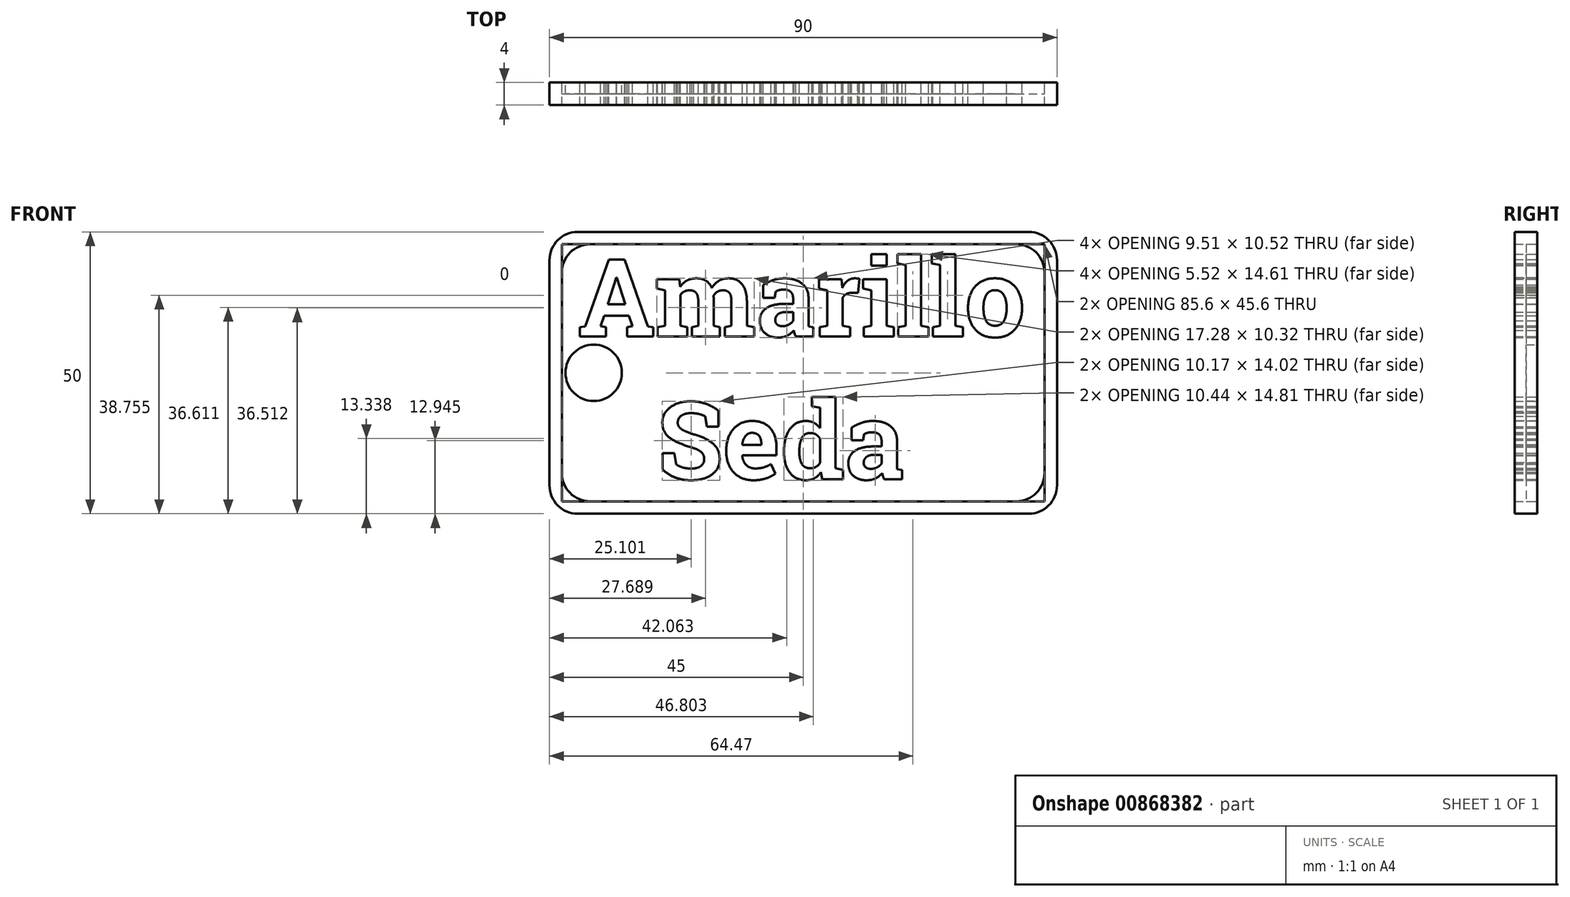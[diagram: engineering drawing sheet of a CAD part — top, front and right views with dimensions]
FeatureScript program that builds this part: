
annotation { "Feature Type Name" : "Feature", "Feature Type Description" : "" }
export const myFeature = defineFeature(function(context is Context, id is Id, definition is map)
    precondition{}
    {
        {
            var Q0;
            Q0=qCreatedBy(makeId("Front.planeOp"),FACE);
            var sketch = newSketch(context, id + "F0", { "sketchPlane" : qUnion([Q0])});
            skLineSegment(sketch, "E0.bottom", {"start": v(-45, 25) * mm, "end": v(45, 25) * mm});
            skLineSegment(sketch, "E0.top", {"start": v(-45, -25) * mm, "end": v(45, -25) * mm});
            skLineSegment(sketch, "E0.left", {"start": v(-45, 25) * mm, "end": v(-45, -25) * mm});
            skLineSegment(sketch, "E0.right", {"start": v(45, 25) * mm, "end": v(45, -25) * mm});
            skLineSegment(sketch, "E1.0", {"start": v(-42.8, 22.8) * mm, "end": v(42.8, 22.8) * mm});
            skLineSegment(sketch, "E1.1", {"start": v(-42.8, 22.8) * mm, "end": v(-42.8, -22.8) * mm});
            skLineSegment(sketch, "E1.2", {"start": v(-42.8, -22.8) * mm, "end": v(42.8, -22.8) * mm});
            skLineSegment(sketch, "E1.3", {"start": v(42.8, 22.8) * mm, "end": v(42.8, -22.8) * mm});
            skText(sketch, "E2", { "text": "Amarillo\n   Seda", "fontName": "RobotoSlab-Bold.ttf"});
            skCircle(sketch, "E3", {"center": v(-37.16, 0) * mm, "radius": 5 * mm});
            const initialGuessF0  = {"E2": [-0.04, 0.00645, 1, 0, 0.01381]};
            skSetInitialGuess(sketch, initialGuessF0);
            skSolve(sketch);
        }
        {
            var Q0;
            Q0=makeQuery(id+"F0.imprint","IMPRINT",FACE,{"disambiguationData":[TD([[makeQuery(id+"F0.imprint","IMPRINT",EDGE,{"derivedFrom":sQuery(id+"F0.wireOp",EDGE,"E2.sketch_text.stroke-16")}),1.0]])]});
            var Q1;
            Q1=makeQuery(id+"F0.imprint","IMPRINT",FACE,{"disambiguationData":[TD([[makeQuery(id+"F0.imprint","IMPRINT",EDGE,{"derivedFrom":sQuery(id+"F0.wireOp",EDGE,"E2.sketch_text.stroke-90")}),1.0]])]});
            var Q2;
            Q2=makeQuery(id+"F0.imprint","IMPRINT",FACE,{"disambiguationData":[TD([[makeQuery(id+"F0.imprint","IMPRINT",EDGE,{"derivedFrom":sQuery(id+"F0.wireOp",EDGE,"E2.sketch_text.stroke-161")}),1.0]])]});
            var Q3;
            Q3=makeQuery(id+"F0.imprint","IMPRINT",FACE,{"disambiguationData":[TD([[makeQuery(id+"F0.imprint","IMPRINT",EDGE,{"derivedFrom":sQuery(id+"F0.wireOp",EDGE,"E2.sketch_text.stroke-281")}),1.0]])]});
            var Q4;
            Q4=makeQuery(id+"F0.imprint","IMPRINT",FACE,{"disambiguationData":[TD([[makeQuery(id+"F0.imprint","IMPRINT",EDGE,{"derivedFrom":sQuery(id+"F0.wireOp",EDGE,"E2.sketch_text.stroke-244")}),1.0]])]});
            var Q5;
            Q5=makeQuery(id+"F0.imprint","IMPRINT",FACE,{"disambiguationData":[TD([[makeQuery(id+"F0.imprint","IMPRINT",EDGE,{"derivedFrom":sQuery(id+"F0.wireOp",EDGE,"E2.sketch_text.stroke-218")}),1.0]])]});
            var Q6;
            Q6=makeQuery(id+"F0.imprint","IMPRINT",FACE,{"disambiguationData":[TD([[makeQuery(id+"F0.imprint","IMPRINT",EDGE,{"derivedFrom":sQuery(id+"F0.wireOp",EDGE,"E1.0")}),-1.0]])]});
            extrude(context, id + "F1", {"entities" : qUnion([Q0, Q1, Q2, Q3, Q4, Q5, Q6]), "depth" : 2 * mm, "offsetDistance" : 25 * mm});
        }
        {
            var Q0;
            Q0=makeQuery(id+"F0.imprint","IMPRINT",FACE,{"disambiguationData":[TD([[makeQuery(id+"F0.imprint","IMPRINT",EDGE,{"derivedFrom":sQuery(id+"F0.wireOp",EDGE,"E2.sketch_text.stroke-0")}),-1.0]])]});
            var Q1;
            Q1=makeQuery(id+"F0.imprint","IMPRINT",FACE,{"disambiguationData":[TD([[makeQuery(id+"F0.imprint","IMPRINT",EDGE,{"derivedFrom":sQuery(id+"F0.wireOp",EDGE,"E2.sketch_text.stroke-20")}),-1.0]])]});
            var Q2;
            Q2=makeQuery(id+"F0.imprint","IMPRINT",FACE,{"disambiguationData":[TD([[makeQuery(id+"F0.imprint","IMPRINT",EDGE,{"derivedFrom":sQuery(id+"F0.wireOp",EDGE,"E2.sketch_text.stroke-63")}),-1.0]])]});
            var Q3;
            Q3=makeQuery(id+"F0.imprint","IMPRINT",FACE,{"disambiguationData":[TD([[makeQuery(id+"F0.imprint","IMPRINT",EDGE,{"derivedFrom":sQuery(id+"F0.wireOp",EDGE,"E2.sketch_text.stroke-98")}),-1.0]])]});
            var Q4;
            Q4=makeQuery(id+"F0.imprint","IMPRINT",FACE,{"disambiguationData":[TD([[makeQuery(id+"F0.imprint","IMPRINT",EDGE,{"derivedFrom":sQuery(id+"F0.wireOp",EDGE,"E2.sketch_text.stroke-117")}),-1.0]])]});
            var Q5;
            Q5=makeQuery(id+"F0.imprint","IMPRINT",FACE,{"disambiguationData":[TD([[makeQuery(id+"F0.imprint","IMPRINT",EDGE,{"derivedFrom":sQuery(id+"F0.wireOp",EDGE,"E2.sketch_text.stroke-127")}),-1.0]])]});
            var Q6;
            Q6=makeQuery(id+"F0.imprint","IMPRINT",FACE,{"disambiguationData":[TD([[makeQuery(id+"F0.imprint","IMPRINT",EDGE,{"derivedFrom":sQuery(id+"F0.wireOp",EDGE,"E2.sketch_text.stroke-131")}),-1.0]])]});
            var Q7;
            Q7=makeQuery(id+"F0.imprint","IMPRINT",FACE,{"disambiguationData":[TD([[makeQuery(id+"F0.imprint","IMPRINT",EDGE,{"derivedFrom":sQuery(id+"F0.wireOp",EDGE,"E2.sketch_text.stroke-141")}),-1.0]])]});
            var Q8;
            Q8=makeQuery(id+"F0.imprint","IMPRINT",FACE,{"disambiguationData":[TD([[makeQuery(id+"F0.imprint","IMPRINT",EDGE,{"derivedFrom":sQuery(id+"F0.wireOp",EDGE,"E2.sketch_text.stroke-151")}),-1.0]])]});
            var Q9;
            Q9=makeQuery(id+"F0.imprint","IMPRINT",FACE,{"disambiguationData":[TD([[makeQuery(id+"F0.imprint","IMPRINT",EDGE,{"derivedFrom":sQuery(id+"F0.wireOp",EDGE,"E2.sketch_text.stroke-254")}),-1.0]])]});
            var Q10;
            Q10=makeQuery(id+"F0.imprint","IMPRINT",FACE,{"disambiguationData":[TD([[makeQuery(id+"F0.imprint","IMPRINT",EDGE,{"derivedFrom":sQuery(id+"F0.wireOp",EDGE,"E2.sketch_text.stroke-225")}),-1.0]])]});
            var Q11;
            Q11=makeQuery(id+"F0.imprint","IMPRINT",FACE,{"disambiguationData":[TD([[makeQuery(id+"F0.imprint","IMPRINT",EDGE,{"derivedFrom":sQuery(id+"F0.wireOp",EDGE,"E2.sketch_text.stroke-201")}),-1.0]])]});
            var Q12;
            Q12=makeQuery(id+"F0.imprint","IMPRINT",FACE,{"disambiguationData":[TD([[makeQuery(id+"F0.imprint","IMPRINT",EDGE,{"derivedFrom":sQuery(id+"F0.wireOp",EDGE,"E2.sketch_text.stroke-171")}),-1.0]])]});
            var Q13;
            Q13=makeQuery(id+"F0.imprint","IMPRINT",FACE,{"disambiguationData":[TD([[makeQuery(id+"F0.imprint","IMPRINT",EDGE,{"derivedFrom":sQuery(id+"F0.wireOp",EDGE,"E0.bottom")}),-1.0]])]});
            extrude(context, id + "F2", {"entities" : qUnion([Q0, Q1, Q2, Q3, Q4, Q5, Q6, Q7, Q8, Q9, Q10, Q11, Q12, Q13]), "depth" : 4 * mm, "offsetDistance" : 25 * mm});
        }
        {
            var Q0;
            Q0=makeQuery(id+"F2.opExtrude","SWEPT_EDGE",EDGE,{"disambiguationData":[OSD([sQuery(id+"F0.wireOp",EDGE,"E0.top"),sQuery(id+"F0.wireOp",EDGE,"E0.left")])]});
            var Q1;
            Q1=makeQuery(id+"F2.opExtrude","SWEPT_EDGE",EDGE,{"disambiguationData":[OSD([sQuery(id+"F0.wireOp",EDGE,"E0.bottom"),sQuery(id+"F0.wireOp",EDGE,"E0.left")])]});
            var Q2;
            Q2=makeQuery(id+"F2.opExtrude","SWEPT_EDGE",EDGE,{"disambiguationData":[OSD([sQuery(id+"F0.wireOp",EDGE,"E1.1"),sQuery(id+"F0.wireOp",EDGE,"E1.2")])]});
            var Q3;
            Q3=makeQuery(id+"F2.opExtrude","SWEPT_EDGE",EDGE,{"disambiguationData":[OSD([sQuery(id+"F0.wireOp",EDGE,"E1.0"),sQuery(id+"F0.wireOp",EDGE,"E1.1")])]});
            var Q4;
            Q4=makeQuery(id+"F2.opExtrude","SWEPT_EDGE",EDGE,{"disambiguationData":[OSD([sQuery(id+"F0.wireOp",EDGE,"E1.0"),sQuery(id+"F0.wireOp",EDGE,"E1.3")])]});
            var Q5;
            Q5=makeQuery(id+"F2.opExtrude","SWEPT_EDGE",EDGE,{"disambiguationData":[OSD([sQuery(id+"F0.wireOp",EDGE,"E1.2"),sQuery(id+"F0.wireOp",EDGE,"E1.3")])]});
            var Q6;
            Q6=makeQuery(id+"F2.opExtrude","SWEPT_EDGE",EDGE,{"disambiguationData":[OSD([sQuery(id+"F0.wireOp",EDGE,"E0.top"),sQuery(id+"F0.wireOp",EDGE,"E0.right")])]});
            var Q7;
            Q7=makeQuery(id+"F2.opExtrude","SWEPT_EDGE",EDGE,{"disambiguationData":[OSD([sQuery(id+"F0.wireOp",EDGE,"E0.bottom"),sQuery(id+"F0.wireOp",EDGE,"E0.right")])]});
            fillet(context, id + "F3", {"entities" : qUnion([Q0, Q1, Q2, Q3, Q4, Q5, Q6, Q7]), "radius" : 5 * mm, "tangentPropagation" : true, "allowEdgeOverflow" : false});
        }
    });
